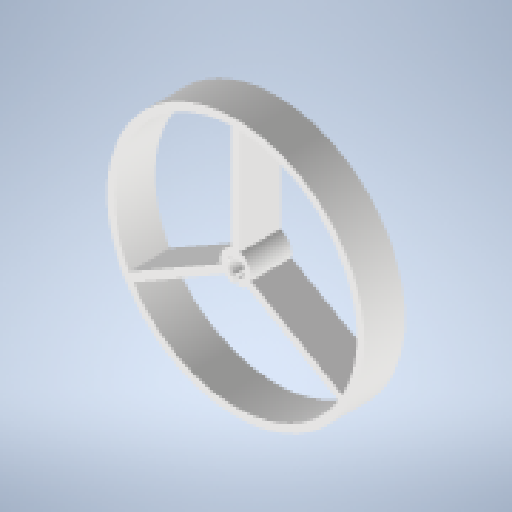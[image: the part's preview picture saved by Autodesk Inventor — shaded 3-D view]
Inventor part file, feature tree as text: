
AUTODESK INVENTOR PART (.ipt)
format: ipt  version: 2025.3 (Build 293356000, 356)  size: 311,296 bytes
history: native  units: mm
features: other x1, extrude x1, pattern_circular x1, chamfer x1
ambient origin geometry x8: Origin, YZ Plane, XZ Plane, XY Plane, X Axis, Y Axis, Z Axis, Center Point
bodies: Body1 (feature_tree)
feature tree (4):
  other  "ソリッド1"
  extrude  "スポーク"  Depth=1.05mm
  pattern_circular  "円形状パターン1"  [2 undecoded]
  chamfer  "面取り1"  Distance=8.0mm
note: 2 required parameter values undecoded (feature->parameter linkage not recoverable at this tier; creation-order binding heuristic only, values carry confidence <= 0.55)
